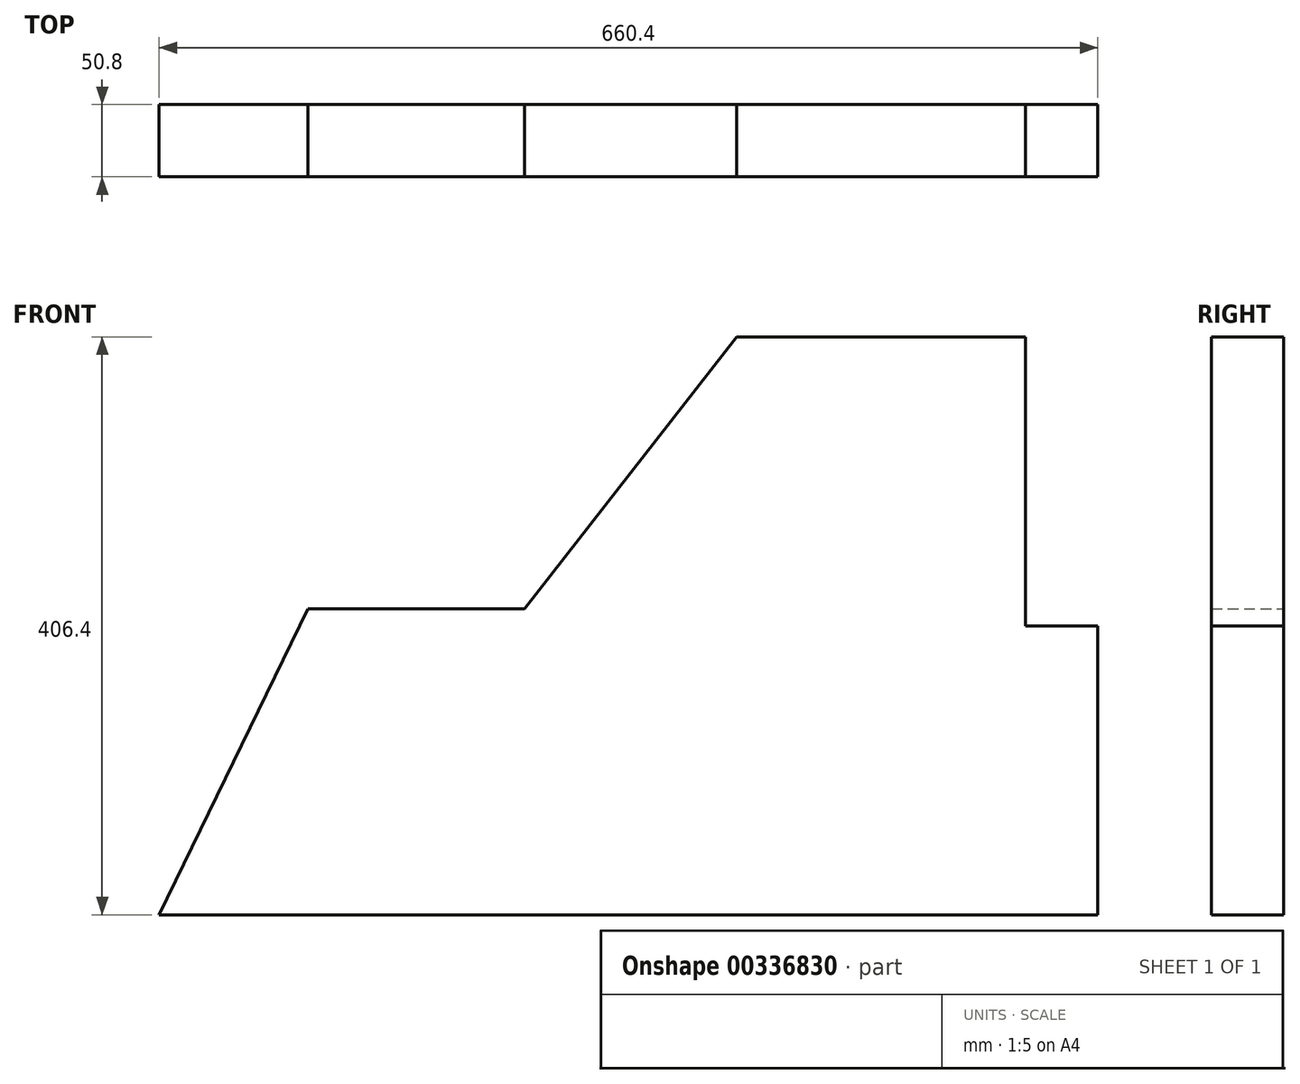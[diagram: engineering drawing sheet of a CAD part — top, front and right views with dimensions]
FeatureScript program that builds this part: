
annotation { "Feature Type Name" : "Feature", "Feature Type Description" : "" }
export const myFeature = defineFeature(function(context is Context, id is Id, definition is map)
    precondition{}
    {
        {
            var Q0;
            Q0=qCreatedBy(makeId("Front.planeOp"),FACE);
            var sketch = newSketch(context, id + "F0", { "sketchPlane" : qUnion([Q0])});
            skLineSegment(sketch, "E0", {"start": v(37.14, 181.38) * mm, "end": v(240.34, 181.38) * mm});
            skLineSegment(sketch, "E1", {"start": v(240.34, 181.38) * mm, "end": v(240.34, -21.82) * mm});
            skLineSegment(sketch, "E2", {"start": v(240.34, -21.82) * mm, "end": v(291.14, -21.82) * mm});
            skLineSegment(sketch, "E3", {"start": v(291.14, -21.82) * mm, "end": v(291.14, -225.02) * mm});
            skLineSegment(sketch, "E4", {"start": v(291.14, -225.02) * mm, "end": v(-369.26, -225.02) * mm});
            skLineSegment(sketch, "E5", {"start": v(-369.26, -225.02) * mm, "end": v(-264.52, -9.76) * mm});
            skLineSegment(sketch, "E6", {"start": v(-264.52, -9.76) * mm, "end": v(-112.12, -9.76) * mm});
            skLineSegment(sketch, "E7", {"start": v(-112.12, -9.76) * mm, "end": v(37.14, 181.38) * mm});
            skSolve(sketch);
        }
        {
            var Q0;
            Q0=makeQuery(id+"F0.imprint","IMPRINT",FACE,{"disambiguationData":[TD([[makeQuery(id+"F0.imprint","IMPRINT",EDGE,{"derivedFrom":sQuery(id+"F0.wireOp",EDGE,"E0")}),-1.0]])]});
            extrude(context, id + "F1", {"entities" : qUnion([Q0]), "depth" : 50.8 * mm});
        }
    });
